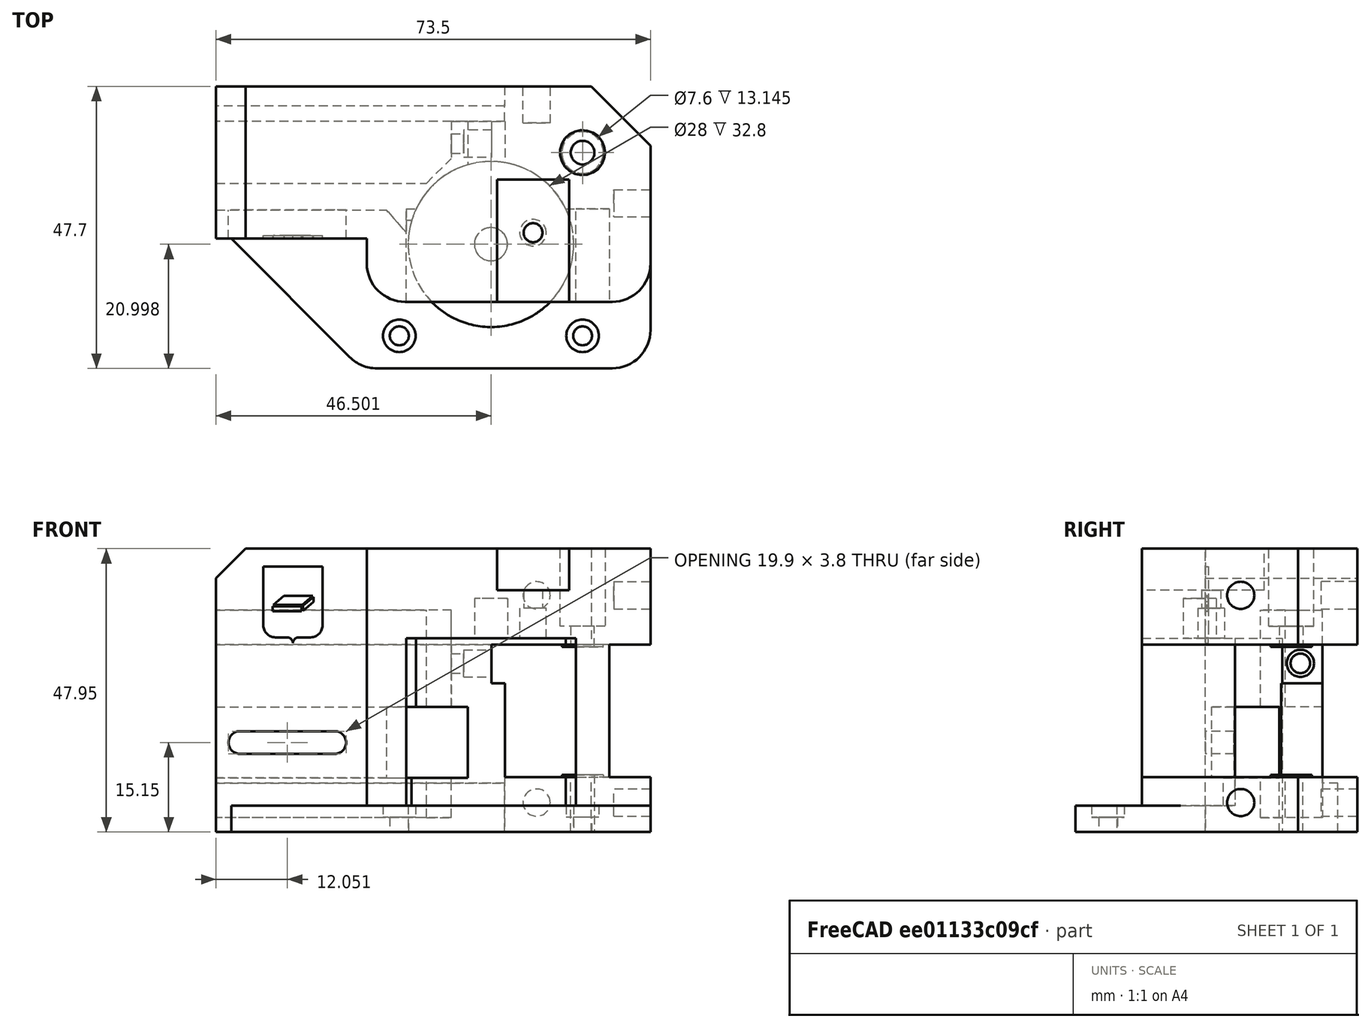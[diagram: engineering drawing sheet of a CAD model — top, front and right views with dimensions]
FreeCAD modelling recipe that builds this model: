
FCSTD DOCUMENT  (FreeCAD 1.0R38641 +468 (Git))
Label: k1_motor_mount_right
License: All rights reserved
LicenseURL: https://en.wikipedia.org/wiki/All_rights_reserved
objects: App::Link×4, Part::Feature×1, PartDesign::FeatureBase×1, PartDesign::Body×1, App::Part×1
note: 4 computed .brp shape members not serialized (recipe doc carries the construction recipe); baked Part::Feature solids carry a one-line shape summary decoded from their .brp
EXTERNAL_REF file=cad_powge_pulley.FCStd obj=Part
EXTERNAL_REF file=cad_20T_15mm_pulley.FCStd obj=Part
EXTERNAL_REF file=cad_nema17_42_60.FCStd obj=COMPOUND049

FEATURE [Part::Feature] Part__Feature  label="step"
  shape: bbox 73.5 x 47.7 x 47.95 mm, 120 faces (baked)
FEATURE [PartDesign::FeatureBase] BaseFeature
  BaseFeature = -> Part__Feature
  Suppressed = false
FEATURE [PartDesign::Body] Body  label="k1_motor_mount_right"
  AllowCompound = false
  BaseFeature = -> Part__Feature
  Group = -> [BaseFeature]
  Origin = -> Origin001
  Placement = pos=(-229,-950,0) rot=(0,0,1;0rad)
  Tip = -> BaseFeature
FEATURE [App::Link] Link  label="cad_powge_pulley_top_link"
  LinkPlacement = pos=(65.1406,50.0783,20.8) rot=(0,0,1;0rad)
  LinkedObject = -> <external cad_powge_pulley.FCStd>#Part
  Placement = pos=(65.1406,50.0783,20.8) rot=(0,0,1;0rad)
FEATURE [App::Link] Link001  label="cad_powge_pulley_bottom_link"
  LinkPlacement = pos=(65.1406,50.0783,9.7) rot=(0,0,1;0rad)
  LinkedObject = -> <external cad_powge_pulley.FCStd>#Part
  Placement = pos=(65.1406,50.0783,9.7) rot=(0,0,1;0rad)
FEATURE [App::Link] Link002  label="cad_20T_pulley_link"
  LinkPlacement = pos=(-37.9821,-34.499,38.8079) rot=(0,0,1;0rad)
  LinkedObject = -> <external cad_20T_15mm_pulley.FCStd>#Part
  Placement = pos=(-37.9821,-34.499,38.8079) rot=(0,0,1;0rad)
FEATURE [App::Link] Link003  label="cad_nema17_link"
  LinkPlacement = pos=(49.6406,34.5783,-16.702) rot=(0,0,1;3.14159rad)
  LinkedObject = -> <external cad_nema17_42_60.FCStd>#COMPOUND049
  Placement = pos=(49.6406,34.5783,-16.702) rot=(0,0,1;3.14159rad)
FEATURE [App::Part] Part  label="k1_motor_mount_right_part"
  Group = -> [Body,Link,Link001,Link002,Link003]
  Origin = -> Origin

RESOLVED EXTERNAL PARTS (link-assembly join: the EXTERNAL_REF files above that resolve inside this repo's crawl, each included once):
---- part cad_powge_pulley.FCStd = doc fcstd_d49da9a9e340 ----
FCSTD DOCUMENT  (FreeCAD 1.0R38641 +468 (Git))
Label: cad_powge_pulley
License: All rights reserved
LicenseURL: https://en.wikipedia.org/wiki/All_rights_reserved
objects: Sketcher::SketchObject×1, PartDesign::Revolution×1, PartDesign::Body×1, App::Part×1
note: 6 computed .brp shape members not serialized (recipe doc carries the construction recipe); baked Part::Feature solids carry a one-line shape summary decoded from their .brp

FEATURE [Sketcher::SketchObject] Sketch
  ArcFitTolerance = 1e-06
  AttachmentSupport = -> [XZ_Plane]
  FullyConstrained = true
  MakeInternals = false
  MapMode = 5
  Placement = pos=(0,0,0) rot=(1,0,0;1.5708rad)
  sketch-geometry (8):
    g0: LineSegment StartX=6.1 StartY=9.3 StartZ=0 EndX=6.1 EndY=1.2 EndZ=0
    g1: LineSegment StartX=6.1 StartY=1.2 StartZ=0 EndX=8 EndY=1.2 EndZ=0
    g2: LineSegment StartX=8 StartY=1.2 StartZ=0 EndX=8 EndY=0 EndZ=0
    g3: LineSegment StartX=8 StartY=0 StartZ=0 EndX=2 EndY=0 EndZ=0
    g4: LineSegment StartX=2 StartY=0 StartZ=0 EndX=2 EndY=10.5 EndZ=0
    g5: LineSegment StartX=2 StartY=10.5 StartZ=0 EndX=8 EndY=10.5 EndZ=0
    g6: LineSegment StartX=8 StartY=10.5 StartZ=0 EndX=8 EndY=9.3 EndZ=0
    g7: LineSegment StartX=8 StartY=9.3 StartZ=0 EndX=6.1 EndY=9.3 EndZ=0
  constraints (24):
    c: Vertical(g0)
    c: Coincident(g1,g0)
    c: Horizontal(g1)
    c: Coincident(g2,g1)
    c: PointOnObject(g2,g-1)
    c: Vertical(g2)
    c: Coincident(g3,g2)
    c: PointOnObject(g3,g-1)
    c: Coincident(g4,g3)
    c: Vertical(g4)
    c: Coincident(g5,g4)
    c: Horizontal(g5)
    c: Coincident(g6,g5)
    c: Vertical(g6)
    c: Coincident(g7,g6)
    c: Horizontal(g7)
    c: Coincident(g0,g7)
    c: Equal(g5,g3)
    c: Equal(g6,g2)
    c: Distance(g4,g-2) = 2
    c: Distance(g5,g-2) = 8
    c: DistanceY(g0,g0) = 8.1
    c: DistanceY(g4,g4) = 10.5
    c: Distance(g0,g-2) = 6.1
FEATURE [PartDesign::Revolution] Revolution
  Angle = 360
  Angle2 = 60
  Axis = (0,2e-16,1)
  Base = (0,0,0)
  Placement = pos=(0,0,0) rot=(1,0,0;1.5708rad)
  Profile = -> Sketch
  ReferenceAxis = -> Sketch [V_Axis]
  Refine = true
  Reversed = true
  Suppressed = false
  Type = 0
FEATURE [PartDesign::Body] Body  label="powge_pulley"
  AllowCompound = false
  Group = -> [Sketch,Revolution]
  Origin = -> Origin
  Tip = -> Revolution
FEATURE [App::Part] Part  label="powge_pulley_part"
  Group = -> [Body]
  Origin = -> Origin001
